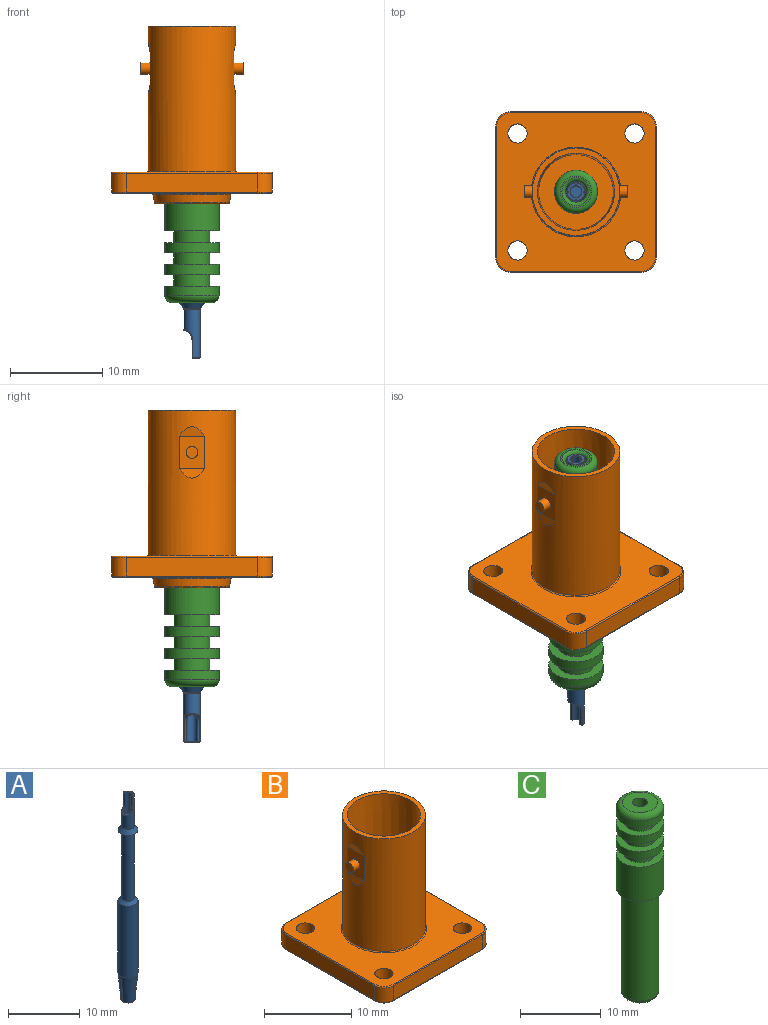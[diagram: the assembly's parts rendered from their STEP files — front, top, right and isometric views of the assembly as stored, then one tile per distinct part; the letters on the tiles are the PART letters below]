
ASSEMBLY  parts=3 mates=2
PART A: 54 faces, bbox 2.8x2.8x35 mm
  f0: cylinder r=0.9mm len=5.25mm, axis (0,0,1), area 21.4mm2, adj f39,f41,f43,f44,f52
  f1: plane 1.7x0.8mm, normal (0,0,1), area 0.6mm2, adj f34,f36,f39,f40
  f2: cylinder r=0.55mm len=3.51mm, axis (0,0,1), area 7mm2, adj f13,f31,f32,f34,f35
  f3: plane 0.9x0.9mm, normal (0,0,-1), area 0.4mm2, adj f18,f21,f46,f49
  f4: plane 0.9x0.9mm, normal (0,0,-1), area 0.4mm2, adj f17,f25,f47,f50
  f5: plane 0.9x0.9mm, normal (0,0,-1), area 0.4mm2, adj f24,f26,f51,f53
  f6: plane 0.9x0.9mm, normal (0,0,-1), area 0.4mm2, adj f20,f23,f45,f48
  f7: cone r=1mm half-angle=5deg, axis (0,0,1), area 32.7mm2, adj f8,f16,f17,f18,f19,f20,f21,f22
  f8: cylinder r=1.4mm len=12.3mm, axis (0,0,1), area 108.2mm2, adj f7,f9
  f9: cone r=0.9mm half-angle=45deg, axis (0,0,-1), area 5.1mm2, adj f8,f10
  f10: cylinder r=0.9mm len=11.63mm, axis (0,0,1), area 65.8mm2, adj f9,f11
  f11: plane 2.8x2.8mm, normal (0,0,-1), area 3.6mm2, adj f10,f12
  f12: cone r=1.4mm half-angle=35.5deg, axis (0,0,-1), area 6.1mm2, adj f11,f52
  f13: plane 1.09x1.09mm, normal (0,0,1), area 0.9mm2, adj f2
  f14: plane 1.72x1.72mm, normal (0,0,-1), area 2.3mm2, adj f15
  f15: cone r=0.6mm half-angle=3deg, axis (0,0,1), area 21.2mm2, adj f14,f16,f17,f18,f19,f20,f21,f22
  f16: plane 0.54x0.1mm, normal (0,0,-1), area 0.1mm2, adj f7,f15,f17,f18
  f17: plane 4x0.75mm, normal (0,-1,0), area 1.9mm2, adj f4,f7,f15,f16,f47,f50
  f18: plane 4x0.75mm, normal (0,1,0), area 1.9mm2, adj f3,f7,f15,f16,f46,f49
  f19: plane 0.54x0.1mm, normal (0,0,-1), area 0.1mm2, adj f7,f15,f20,f21
  f20: plane 4x0.75mm, normal (-1,0,0), area 1.9mm2, adj f6,f7,f15,f19,f45,f48
  f21: plane 4x0.75mm, normal (1,0,0), area 1.9mm2, adj f3,f7,f15,f19,f46,f49
  f22: plane 0.54x0.1mm, normal (0,0,-1), area 0.1mm2, adj f7,f15,f23,f24
  f23: plane 4x0.75mm, normal (0,1,0), area 1.9mm2, adj f6,f7,f15,f22,f45,f48
  f24: plane 4x0.75mm, normal (0,-1,0), area 1.9mm2, adj f5,f7,f15,f22,f51,f53
  f25: plane 4x0.75mm, normal (1,0,0), area 1.9mm2, adj f4,f7,f15,f27,f47,f50
  f26: plane 4x0.75mm, normal (-1,0,0), area 1.9mm2, adj f5,f7,f15,f27,f51,f53
  f27: plane 0.54x0.1mm, normal (0,0,-1), area 0.1mm2, adj f7,f15,f25,f26
  f28: cylinder r=1mm len=1.7mm, axis (0,-1,0), area 0.9mm2, adj f29,f30,f32,f43
  f29: plane 1.97x0.26mm, normal (-1,0,0), area 0.5mm2, adj f28,f31,f36,f41
  f30: plane 1.97x0.26mm, normal (-1,0,0), area 0.5mm2, adj f28,f35,f40,f44
  f31: cylinder r=0.05mm len=1.97mm, axis (0,0,1), area 0.1mm2, adj f2,f29,f32,f33
  f32: bspline ~1.19x1.17mm, area 0.3mm2, adj f2,f28,f31,f35
  f33: sphere r=0.05mm, area 0mm2, adj f31,f34,f36
  f34: torus R=0.6mm, axis (0,0,-1), area 0.1mm2, adj f1,f2,f33,f37
  f35: cylinder r=0.05mm len=1.97mm, axis (0,0,1), area 0.1mm2, adj f2,f30,f32,f37
  f36: cylinder r=0.05mm len=0.26mm, axis (0,-1,0), area 0mm2, adj f1,f29,f33,f38
  f37: sphere r=0.05mm, area 0mm2, adj f34,f35,f40
  f38: sphere r=0.05mm, area 0mm2, adj f36,f39,f41
  f39: torus R=0.85mm, axis (0,0,-1), area 0.2mm2, adj f0,f1,f38,f42
  f40: cylinder r=0.05mm len=0.26mm, axis (0,-1,0), area 0mm2, adj f1,f30,f37,f42
  f41: cylinder r=0.05mm len=1.97mm, axis (0,0,1), area 0.2mm2, adj f0,f29,f38,f43
  f42: sphere r=0.05mm, area 0mm2, adj f39,f40,f44
  f43: bspline ~1.8x1.28mm, area 0.3mm2, adj f0,f28,f41,f44
  f44: cylinder r=0.05mm len=1.97mm, axis (0,0,1), area 0.2mm2, adj f0,f30,f42,f43
  f45: torus R=0.95mm, axis (0,0,-1), area 0.1mm2, adj f6,f7,f20,f23
  f46: torus R=0.95mm, axis (0,0,-1), area 0.1mm2, adj f3,f7,f18,f21
  f47: torus R=0.95mm, axis (0,0,-1), area 0.1mm2, adj f4,f7,f17,f25
  f48: torus R=0.65mm, axis (0,0,-1), area 0.1mm2, adj f6,f15,f20,f23
  f49: torus R=0.65mm, axis (0,0,-1), area 0.1mm2, adj f3,f15,f18,f21
  f50: torus R=0.65mm, axis (0,0,-1), area 0.1mm2, adj f4,f15,f17,f25
  f51: torus R=0.95mm, axis (0,0,-1), area 0.1mm2, adj f5,f7,f24,f26
  f52: torus R=0.95mm, axis (0,0,1), area 0.2mm2, adj f0,f12
  f53: torus R=0.65mm, axis (0,0,-1), area 0.1mm2, adj f5,f15,f24,f26
PART B: 54 faces, bbox 17.7x17.7x19.3 mm
  f0: cylinder r=4.75mm len=15.75mm, axis (0,0,-1), area 442.7mm2, adj f15,f34,f37,f38,f39,f40,f41,f42
  f1: plane 17.2x17.2mm, normal (0,0,-1), area 220.5mm2, adj f11,f12,f13,f14,f18,f19,f20,f21
  f2: plane 17.2x17.2mm, normal (0,0,1), area 205.5mm2, adj f11,f12,f13,f14,f26,f27,f28,f29
  f3: cylinder r=1.59mm len=2.03mm, axis (0,0,1), area 5.1mm2, adj f4,f10,f18,f29
  f4: plane 14.28x2.03mm, normal (0,-1,0), area 29mm2, adj f3,f5,f20,f27
  f5: cylinder r=1.59mm len=2.03mm, axis (0,0,1), area 5.1mm2, adj f4,f6,f22,f26
  f6: plane 14.28x2.03mm, normal (-1,0,0), area 29mm2, adj f5,f7,f24,f28
  f7: cylinder r=1.59mm len=2.03mm, axis (0,0,1), area 5.1mm2, adj f6,f8,f25,f30
  f8: plane 14.28x2.03mm, normal (0,1,0), area 29mm2, adj f7,f9,f23,f32
  f9: cylinder r=1.59mm len=2.03mm, axis (0,0,1), area 5.1mm2, adj f8,f10,f21,f33
  f10: plane 14.28x2.03mm, normal (1,0,0), area 29mm2, adj f3,f9,f19,f31
  f11: cylinder r=1.04mm len=2.29mm, axis (0,0,1), area 15mm2, adj f1,f2
  f12: cylinder r=1.04mm len=2.29mm, axis (0,0,1), area 15mm2, adj f1,f2
  f13: cylinder r=1.04mm len=2.29mm, axis (0,0,1), area 15mm2, adj f1,f2
  f14: cylinder r=1.04mm len=2.29mm, axis (0,0,1), area 15mm2, adj f1,f2
  f15: plane 9.5x9.5mm, normal (0,0,1), area 15.7mm2, adj f0,f47
  f16: cone r=4.25mm half-angle=10deg, axis (0,0,1), area 24.7mm2, adj f35,f36
  f17: plane 7.89x7.89mm, normal (0,0,-1), area 21.7mm2, adj f35,f53
  f18: torus R=1.46mm, axis (0,0,-1), area 0.5mm2, adj f1,f3,f19,f20
  f19: cylinder r=0.13mm len=14.28mm, axis (0,1,0), area 2.8mm2, adj f1,f10,f18,f21
  f20: cylinder r=0.13mm len=14.28mm, axis (1,0,0), area 2.8mm2, adj f1,f4,f18,f22
  f21: torus R=1.46mm, axis (0,0,-1), area 0.5mm2, adj f1,f9,f19,f23
  f22: torus R=1.46mm, axis (0,0,-1), area 0.5mm2, adj f1,f5,f20,f24
  f23: cylinder r=0.13mm len=14.28mm, axis (-1,0,0), area 2.8mm2, adj f1,f8,f21,f25
  f24: cylinder r=0.13mm len=14.28mm, axis (0,-1,0), area 2.8mm2, adj f1,f6,f22,f25
  f25: torus R=1.46mm, axis (0,0,-1), area 0.5mm2, adj f1,f7,f23,f24
  f26: torus R=1.46mm, axis (0,0,-1), area 0.5mm2, adj f2,f5,f27,f28
  f27: cylinder r=0.13mm len=14.28mm, axis (-1,0,0), area 2.8mm2, adj f2,f4,f26,f29
  f28: cylinder r=0.13mm len=14.28mm, axis (0,1,0), area 2.8mm2, adj f2,f6,f26,f30
  f29: torus R=1.46mm, axis (0,0,-1), area 0.5mm2, adj f2,f3,f27,f31
  f30: torus R=1.46mm, axis (0,0,-1), area 0.5mm2, adj f2,f7,f28,f32
  f31: cylinder r=0.13mm len=14.28mm, axis (0,-1,0), area 2.8mm2, adj f2,f10,f29,f33
  f32: cylinder r=0.13mm len=14.28mm, axis (1,0,0), area 2.8mm2, adj f2,f8,f30,f33
  f33: torus R=1.46mm, axis (0,0,-1), area 0.5mm2, adj f2,f9,f31,f32
  f34: torus R=4.88mm, axis (0,0,-1), area 6mm2, adj f0,f2
  f35: torus R=3.95mm, axis (0,0,-1), area 4.5mm2, adj f16,f17
  f36: torus R=4.36mm, axis (0,0,-1), area 4.8mm2, adj f1,f16
  f37: plane 3.51x2.75mm, normal (-1,0,0), area 8.4mm2, adj f0,f38,f39,f45
  f38: plane 2.75x1.04mm, normal (-0.98,0,0.19), area 2mm2, adj f0,f37
  f39: plane 2.75x1.04mm, normal (-0.98,0,-0.19), area 2mm2, adj f0,f37
  f40: plane 2.75x1.04mm, normal (0.98,0,0.19), area 2mm2, adj f0,f41
  f41: plane 3.51x2.75mm, normal (1,0,0), area 8.4mm2, adj f0,f40,f42,f44
  f42: plane 2.75x1.04mm, normal (0.98,0,-0.19), area 2mm2, adj f0,f41
  f43: plane 1.27x1.27mm, normal (1,0,0), area 1.3mm2, adj f44
  f44: cylinder r=0.64mm len=1.27mm, axis (1,0,0), area 4.2mm2, adj f41,f43
  f45: cylinder r=0.64mm len=1.27mm, axis (1,0,0), area 4.2mm2, adj f37,f46
  f46: plane 1.27x1.27mm, normal (-1,0,0), area 1.3mm2, adj f45
  f47: cone r=4.06mm half-angle=0.5deg, axis (0,0,1), area 411.7mm2, adj f15,f48
  f48: plane 8.13x8.13mm, normal (0,0,1), area 34.7mm2, adj f47,f49
  f49: cylinder r=2.34mm len=4.67mm, axis (0,0,-1), area 16.8mm2, adj f48,f50
  f50: plane 7.11x7.11mm, normal (0,0,-1), area 22.6mm2, adj f49,f51
  f51: cylinder r=3.56mm len=7.11mm, axis (0,0,-1), area 39.7mm2, adj f50,f52
  f52: plane 7.11x7.11mm, normal (0,0,1), area 12.5mm2, adj f51,f53
  f53: cylinder r=2.95mm len=5.89mm, axis (0,0,-1), area 9.4mm2, adj f17,f52
PART C: 23 faces, bbox 6.4x6.4x29.2 mm
  f0: plane 3.4x3.4mm, normal (0,0,-1), area 1.8mm2, adj f1,f22
  f1: torus R=1.7mm, axis (0,0,-1), area 13.2mm2, adj f0,f2
  f2: cylinder r=2.34mm len=15.52mm, axis (0,0,-1), area 227.9mm2, adj f1,f3
  f3: plane 5.89x5.89mm, normal (0,0,-1), area 10.1mm2, adj f2,f4
  f4: cylinder r=2.95mm len=5.89mm, axis (0,0,-1), area 96.8mm2, adj f3,f5
  f5: plane 5.89x5.89mm, normal (0,0,1), area 15.3mm2, adj f4,f6
  f6: cylinder r=1.96mm len=3.91mm, axis (0,0,-1), area 15.6mm2, adj f5,f7
  f7: plane 5.89x5.89mm, normal (0,0,-1), area 15.3mm2, adj f6,f8
  f8: cylinder r=2.95mm len=5.89mm, axis (0,0,-1), area 20.2mm2, adj f7,f9
  f9: plane 5.89x5.89mm, normal (0,0,1), area 15.3mm2, adj f8,f10
  f10: cylinder r=1.96mm len=3.91mm, axis (0,0,-1), area 15.6mm2, adj f9,f11
  f11: plane 5.89x5.89mm, normal (0,0,-1), area 15.3mm2, adj f10,f12
  f12: cylinder r=2.95mm len=5.89mm, axis (0,0,-1), area 20.7mm2, adj f11,f13
  f13: plane 5.89x5.89mm, normal (0,0,1), area 15.3mm2, adj f12,f14
  f14: cylinder r=1.96mm len=3.91mm, axis (0,0,-1), area 15.6mm2, adj f13,f15
  f15: plane 5.89x5.89mm, normal (0,0,-1), area 15.3mm2, adj f14,f16
  f16: cylinder r=2.95mm len=5.89mm, axis (0,0,-1), area 18.3mm2, adj f15,f17
  f17: torus R=2.18mm, axis (0,0,-1), area 20.1mm2, adj f16,f18
  f18: plane 4.37x4.37mm, normal (0,0,1), area 12.4mm2, adj f17,f19
  f19: cylinder r=0.91mm len=11.63mm, axis (0,0,-1), area 66.8mm2, adj f18,f20
  f20: cone r=1.14mm half-angle=45deg, axis (0,0,-1), area 2.1mm2, adj f19,f21
  f21: cylinder r=1.14mm len=16.92mm, axis (0,0,-1), area 121.5mm2, adj f20,f22
  f22: torus R=1.52mm, axis (0,0,-1), area 4.8mm2, adj f0,f21
PLACE A rot(axis=(1,0,0),180deg) t=(0,0,-13)mm
PLACE B at identity
PLACE C rot(axis=(1,0,0),180deg) t=(0,0,0)mm
MATE fastened A.f0 <-> C.f1  axis (0,0,1) through (0,0,-13)mm
MATE fastened C.f1 <-> B.f47  axis (0,0,1) through (0,0,0)mm
